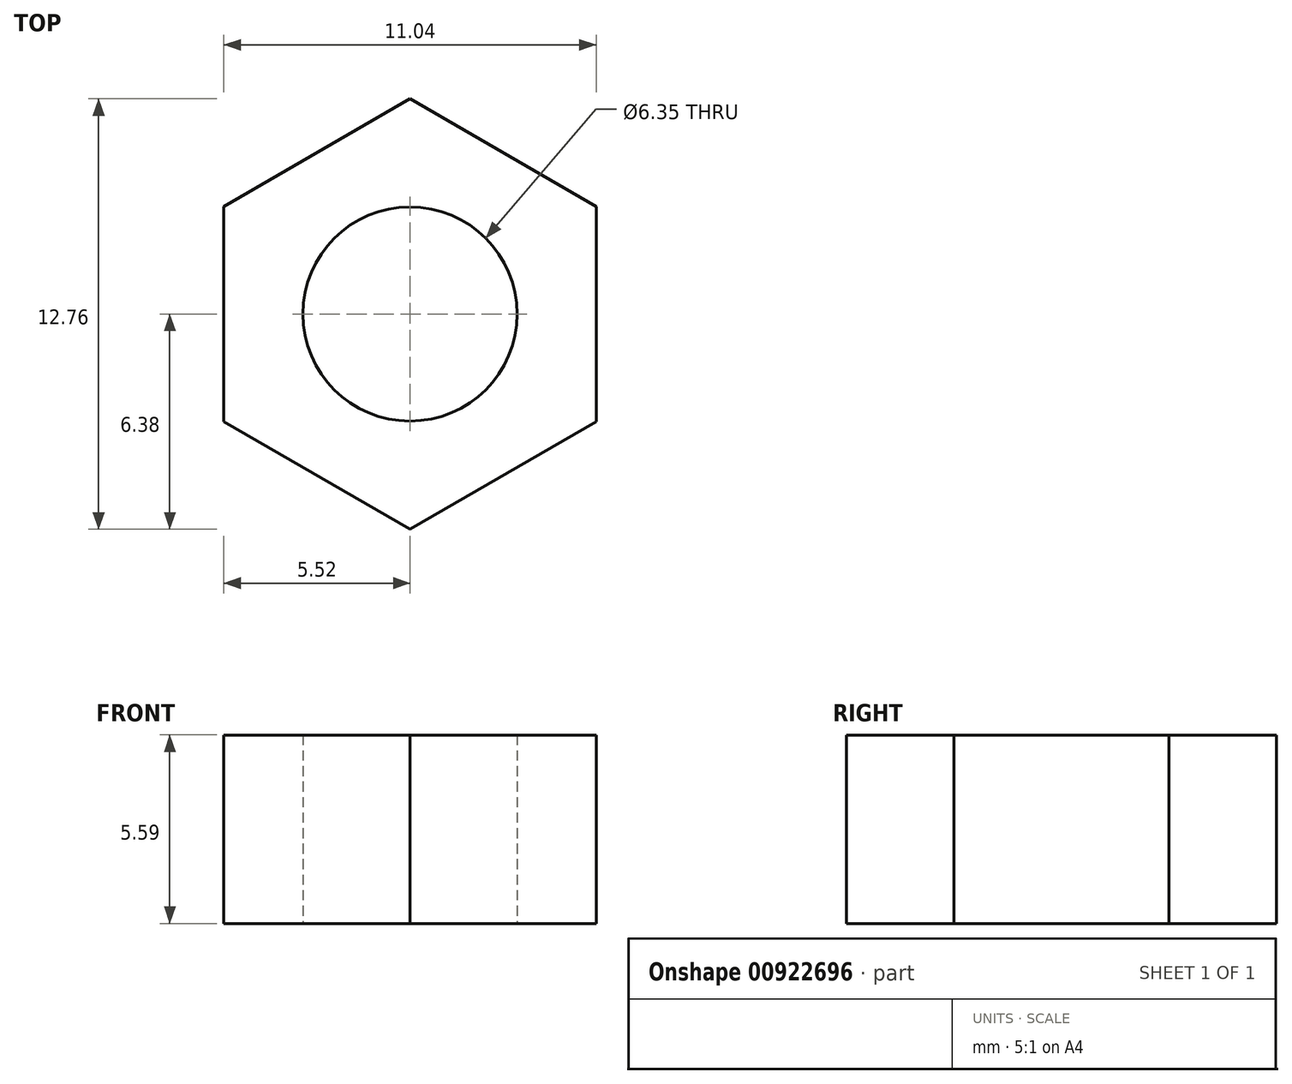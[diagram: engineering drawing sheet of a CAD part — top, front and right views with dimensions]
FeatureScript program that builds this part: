
annotation { "Feature Type Name" : "Feature", "Feature Type Description" : "" }
export const myFeature = defineFeature(function(context is Context, id is Id, definition is map)
    precondition{}
    {
        {
            var Q0;
            Q0=qCreatedBy(makeId("Top.planeOp"),FACE);
            var sketch = newSketch(context, id + "F0", { "sketchPlane" : qUnion([Q0])});
            skCircle(sketch, "E0.cCircle", {"center": v(0, 0) * mm, "radius": 5.52 * mm, "construction": true});
            skLineSegment(sketch, "E0.0", {"start": v(5.52, -3.19) * mm, "end": v(0, -6.38) * mm});
            skLineSegment(sketch, "E0.1", {"start": v(0, -6.38) * mm, "end": v(-5.52, -3.19) * mm});
            skLineSegment(sketch, "E0.2", {"start": v(-5.52, -3.19) * mm, "end": v(-5.52, 3.19) * mm});
            skLineSegment(sketch, "E0.3", {"start": v(-5.52, 3.19) * mm, "end": v(0, 6.38) * mm});
            skLineSegment(sketch, "E0.4", {"start": v(0, 6.38) * mm, "end": v(5.52, 3.19) * mm});
            skLineSegment(sketch, "E0.5", {"start": v(5.52, 3.19) * mm, "end": v(5.52, -3.19) * mm});
            skPoint(sketch, "E0.0.midPoint", {"position": v(2.76, -4.78) * mm});
            skCircle(sketch, "E1", {"center": v(0, 0) * mm, "radius": 3.18 * mm});
            skSolve(sketch);
        }
        {
            var Q0;
            Q0 = qSketchRegion(id + "F0", true);
            extrude(context, id + "F1", {"entities" : qUnion([Q0]), "depth" : 5.6 * mm, "offsetDistance" : 25.4 * mm});
        }
    });
